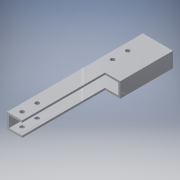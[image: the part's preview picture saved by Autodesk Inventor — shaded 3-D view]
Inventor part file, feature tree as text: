
AUTODESK INVENTOR PART (.ipt)
format: ipt  version: 2016 (Build 200138000, 138)  size: 139,264 bytes
history: native  units: in
note: dims shown in document units (in); Inventor stores cm internally (conversion verified against a paired STEP export)
features: extrude x4, sketch x4
ambient origin geometry x8: Origin, YZ Plane, XZ Plane, XY Plane, X Axis, Y Axis, Z Axis, Center Point
bodies: Solid1 (feature_tree)
feature tree (8):
  extrude  "Extrusion1"  Depth=1.0in
  extrude  "Extrusion2"  Depth=9.0in TaperAngle=0.0deg
  extrude  "Extrusion3"  Depth=5.5in
  extrude  "Extrusion4"  Depth=1.0in
  sketch  "Sketch1"  dims[d0=2.0in d1=1.0in]
  sketch  "Sketch2"  dims[d2=0.125in d3=9.0in d4=0.0in]
  sketch  "Sketch3"  dims[d5=1.0in d6=5.5in]
  sketch  "Sketch4"  dims[d7=1.0in d8=0.0in d9=0.2656in d10=0.2656in d11=0.5in d12=0.5in d13=0.5in d14=1.5in d15=1.0in d16=0.0in d17=0.2656in d18=0.266in d19=2.0in d20=0.5in d21=0.5in d22=1.0in d23=1.0in d24=0.0in]
